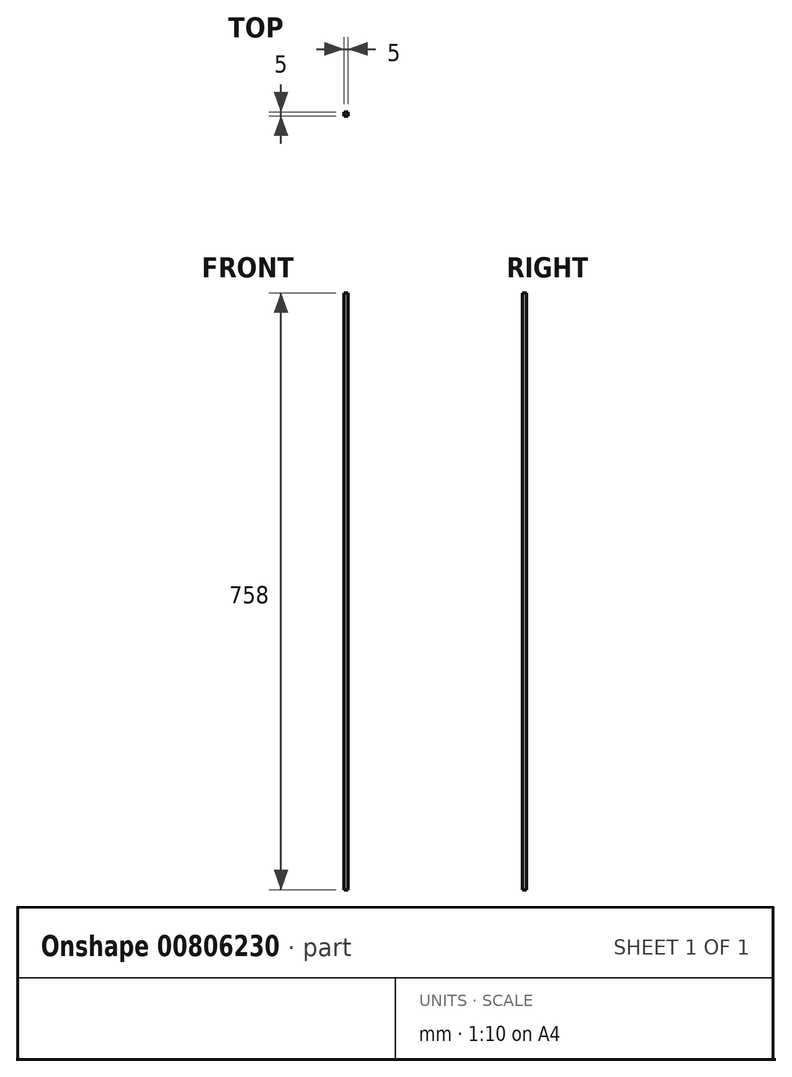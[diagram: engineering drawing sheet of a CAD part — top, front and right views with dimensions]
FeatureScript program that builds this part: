
annotation { "Feature Type Name" : "Feature", "Feature Type Description" : "" }
export const myFeature = defineFeature(function(context is Context, id is Id, definition is map)
    precondition{}
    {
        {
            var Q0;
            Q0=qCreatedBy(makeId("Top.planeOp"),FACE);
            var sketch = newSketch(context, id + "F0", { "sketchPlane" : qUnion([Q0])});
            skLineSegment(sketch, "E0.bottom", {"start": v(0, 0) * mm, "end": v(5, 0) * mm});
            skLineSegment(sketch, "E0.top", {"start": v(0, 5) * mm, "end": v(5, 5) * mm});
            skLineSegment(sketch, "E0.left", {"start": v(0, 0) * mm, "end": v(0, 5) * mm});
            skLineSegment(sketch, "E0.right", {"start": v(5, 0) * mm, "end": v(5, 5) * mm});
            skSolve(sketch);
        }
        {
            var Q0;
            Q0=qSketchRegion(id+"F0",true);
            extrude(context, id + "F1", {"entities" : qUnion([Q0]), "depth" : 758 * mm, "offsetDistance" : 25 * mm});
        }
    });
